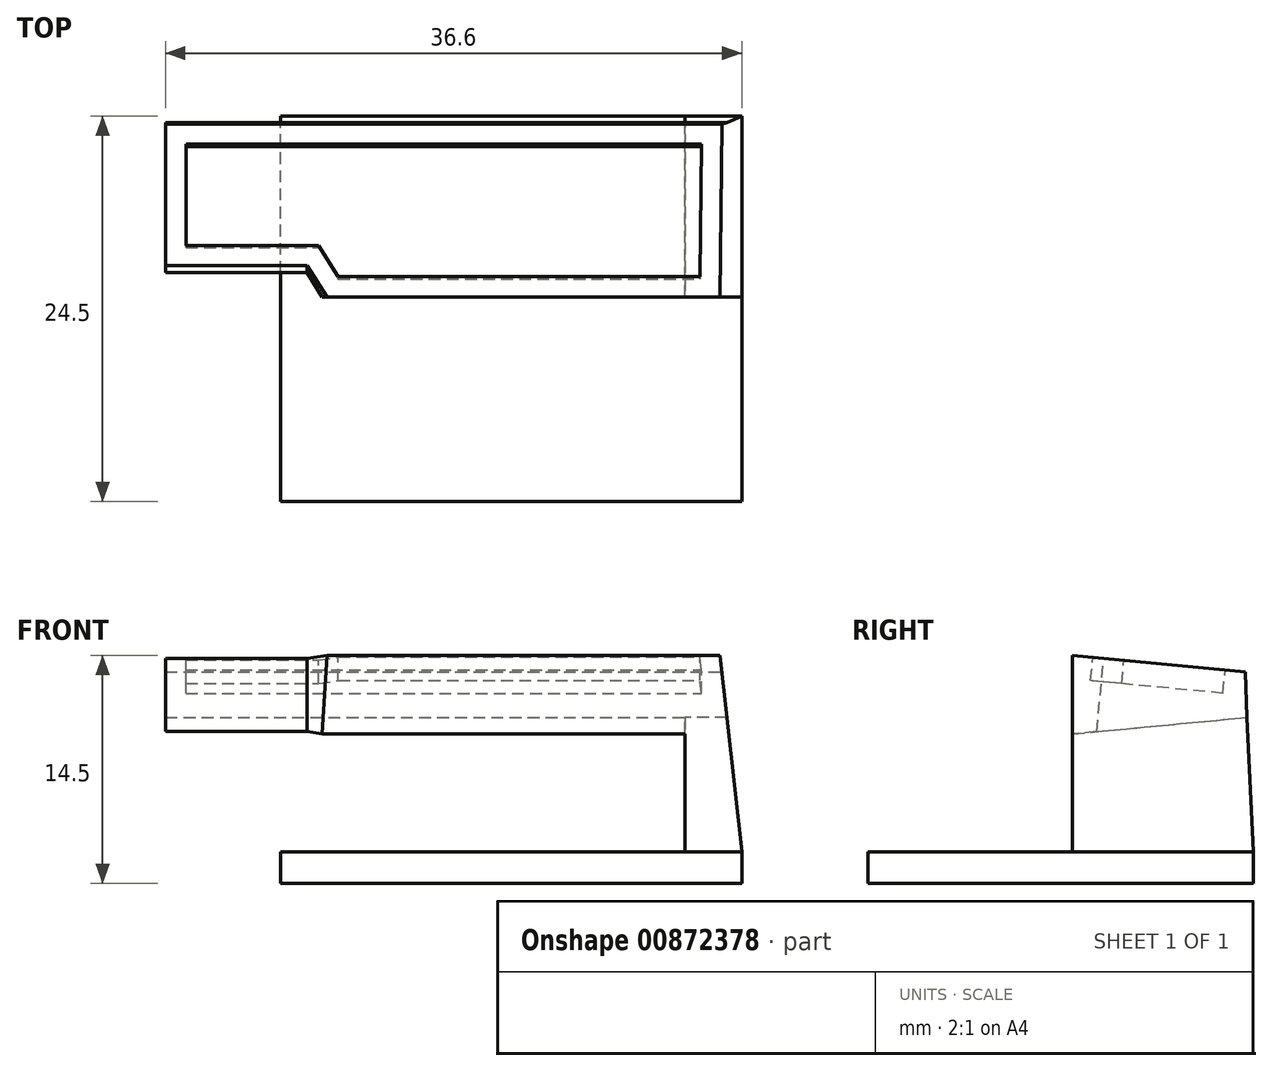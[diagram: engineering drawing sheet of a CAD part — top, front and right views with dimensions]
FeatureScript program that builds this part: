
annotation { "Feature Type Name" : "Feature", "Feature Type Description" : "" }
export const myFeature = defineFeature(function(context is Context, id is Id, definition is map)
    precondition{}
    {
        {
            var Q0;
            Q0=qCreatedBy(makeId("Top.planeOp"),FACE);
            var sketch = newSketch(context, id + "F0", { "sketchPlane" : qUnion([Q0])});
            skLineSegment(sketch, "E0.bottom", {"start": v(0, 0) * mm, "end": v(29.3, 0) * mm});
            skLineSegment(sketch, "E0.top", {"start": v(0, 24.5) * mm, "end": v(29.3, 24.5) * mm});
            skLineSegment(sketch, "E0.left", {"start": v(0, 0) * mm, "end": v(0, 24.5) * mm});
            skLineSegment(sketch, "E0.right", {"start": v(29.3, 0) * mm, "end": v(29.3, 24.5) * mm});
            skSolve(sketch);
        }
        {
            var Q0;
            Q0 = qSketchRegion(id + "F0", true);
            extrude(context, id + "F1", {"entities" : qUnion([Q0]), "depth" : 2 * mm, "offsetDistance" : 25 * mm});
        }
        {
            var Q0;
            Q0=makeQuery(id+"F1.opExtrude","CAP_FACE",FACE,{"disambiguationData":[OSD([sQuery(id+"F0.wireOp",EDGE,"E0.bottom"),sQuery(id+"F0.wireOp",EDGE,"E0.top"),sQuery(id+"F0.wireOp",EDGE,"E0.left"),sQuery(id+"F0.wireOp",EDGE,"E0.right")])],"isStart":false});
            var sketch = newSketch(context, id + "F2", { "sketchPlane" : qUnion([Q0])});
            skLineSegment(sketch, "E1.bottom", {"start": v(29.3, 24.5) * mm, "end": v(25.7, 24.5) * mm});
            skLineSegment(sketch, "E1.top", {"start": v(29.3, 13) * mm, "end": v(25.7, 13) * mm});
            skLineSegment(sketch, "E1.left", {"start": v(29.3, 24.5) * mm, "end": v(29.3, 13) * mm});
            skLineSegment(sketch, "E1.right", {"start": v(25.7, 24.5) * mm, "end": v(25.7, 13) * mm});
            skSolve(sketch);
        }
        {
            var Q0;
            {var subQ4=sQuery(id+"F2.wireOp",EDGE,"E1.top");Q0=makeQuery(id+"F2.imprint","IMPRINT",FACE,{"disambiguationData":[TD([[makeQuery(id+"F2.imprint","IMPRINT",EDGE,{"derivedFrom":subQ4}),1.0]])]});}
            cPlane(context, id + "F3", {"entities" : qUnion([Q0]), "cplaneType" : CPlaneType.OFFSET, "offset" : 10 * mm, "width" : 150 * mm, "height" : 150 * mm});
        }
        {
            var Q0;
            Q0=qCreatedBy(id+"F3.planeOp",FACE);
            var sketch = newSketch(context, id + "F4", { "sketchPlane" : qUnion([Q0])});
            skLineSegment(sketch, "E2.bottom", {"start": v(28.2, 24) * mm, "end": v(25.7, 24) * mm});
            skLineSegment(sketch, "E2.top", {"start": v(28.2, 13) * mm, "end": v(25.7, 13) * mm});
            skLineSegment(sketch, "E2.left", {"start": v(28.2, 24) * mm, "end": v(28.2, 13) * mm});
            skLineSegment(sketch, "E2.right", {"start": v(25.7, 24) * mm, "end": v(25.7, 13) * mm});
            skSolve(sketch);
        }
        {
            var Q1;
            Q1 = qSketchRegion(id + "F4", true);
            var Q2;
            Q2 = qSketchRegion(id + "F2", true);
            loft(context, id + "F5", {"operationType" : NewBodyOperationType.ADD, "sheetProfilesArray" : [{ "sheetProfileEntities" : qUnion([Q1]) }, { "sheetProfileEntities" : qUnion([Q2]) }]});
        }
        {
            var Q0;
            Q0=makeQuery(id+"F5.opLoft","SWEPT_FACE",FACE,{"disambiguationData":[OSD([sQuery(id+"F0.wireOp",EDGE,"E0.top"),sQuery(id+"F2.wireOp",EDGE,"E1.bottom"),sQuery(id+"F2.wireOp",EDGE,"E1.top"),sQuery(id+"F2.wireOp",EDGE,"E1.right"),sQuery(id+"F4.wireOp",EDGE,"E2.bottom"),sQuery(id+"F4.wireOp",EDGE,"E2.top"),sQuery(id+"F4.wireOp",EDGE,"E2.right")])]});
            var sketch = newSketch(context, id + "F6", { "sketchPlane" : qUnion([Q0])});
            skLineSegment(sketch, "E3", {"start": v(-13, 12) * mm, "end": v(-13, 9.5) * mm});
            skLineSegment(sketch, "E4", {"start": v(-13, 14.5) * mm, "end": v(-13, 12) * mm});
            skLineSegment(sketch, "E5", {"start": v(-13, 9.5) * mm, "end": v(-24.07, 10.55) * mm});
            skLineSegment(sketch, "E6", {"start": v(-24.07, 10.55) * mm, "end": v(-24, 13.45) * mm});
            skLineSegment(sketch, "E7", {"start": v(-24, 13.45) * mm, "end": v(-13, 14.5) * mm});
            skSolve(sketch);
        }
        {
            var Q0;
            Q0 = qSketchRegion(id + "F6", true);
            extrude(context, id + "F7", {"entities" : qUnion([Q0]), "operationType" : NewBodyOperationType.ADD, "depth" : 33 * mm, "offsetDistance" : 25 * mm});
        }
        {
            var Q0;
            Q0=makeQuery(id+"F7.opExtrude","CAP_FACE",FACE,{"disambiguationData":[OSD([sQuery(id+"F6.wireOp",EDGE,"E3"),sQuery(id+"F6.wireOp",EDGE,"E4"),sQuery(id+"F6.wireOp",EDGE,"E5"),sQuery(id+"F6.wireOp",EDGE,"E6"),sQuery(id+"F6.wireOp",EDGE,"E7")])],"isStart":true});
            var Q1;
            Q1=makeQuery(id+"F5.opLoft","SWEPT_FACE",FACE,{"disambiguationData":[OSD([sQuery(id+"F0.wireOp",EDGE,"E0.right"),sQuery(id+"F2.wireOp",EDGE,"E1.bottom"),sQuery(id+"F2.wireOp",EDGE,"E1.top"),sQuery(id+"F2.wireOp",EDGE,"E1.left"),sQuery(id+"F4.wireOp",EDGE,"E2.bottom"),sQuery(id+"F4.wireOp",EDGE,"E2.top"),sQuery(id+"F4.wireOp",EDGE,"E2.left")])]});
            extrude(context, id + "F8", {"entities" : qUnion([Q0]), "operationType" : NewBodyOperationType.ADD, "endBound" : BoundingType.UP_TO_SURFACE, "depth" : 25 * mm, "endBoundEntityFace" : qUnion([Q1]), "offsetDistance" : 25 * mm});
        }
        {
            var Q0;
            {var subQ0=sQuery(id+"F6.wireOp",EDGE,"E7");Q0=makeQuery(id+"F8.boolean.opBoolean","MERGE",FACE,{"derivedFrom":[makeQuery(id+"F7.opExtrude","SWEPT_FACE",FACE,{"disambiguationData":[OSD([subQ0])]}),makeQuery(id+"F8.opExtrude","SWEPT_FACE",FACE,{"disambiguationData":[OSD([subQ0])]})]});}
            var sketch = newSketch(context, id + "F9", { "sketchPlane" : qUnion([Q0])});
            skLineSegment(sketch, "E8", {"start": v(-7.3, 11.56) * mm, "end": v(-7.3, 13.56) * mm});
            skLineSegment(sketch, "E9", {"start": v(-7.3, 13.56) * mm, "end": v(1.7, 13.56) * mm});
            skLineSegment(sketch, "E10", {"start": v(1.7, 13.56) * mm, "end": v(2.95, 11.56) * mm});
            skLineSegment(sketch, "E11", {"start": v(2.95, 11.56) * mm, "end": v(-7.3, 11.56) * mm});
            skSolve(sketch);
        }
        {
            var Q0;
            Q0 = qSketchRegion(id + "F9", true);
            var Q1;
            Q1=makeQuery(id+"F7.opExtrude","SWEPT_FACE",FACE,{"disambiguationData":[OSD([sQuery(id+"F6.wireOp",EDGE,"E5")])]});
            extrude(context, id + "F10", {"entities" : qUnion([Q0]), "operationType" : NewBodyOperationType.REMOVE, "endBound" : BoundingType.UP_TO_SURFACE, "oppositeDirection" : true, "depth" : 25 * mm, "endBoundEntityFace" : qUnion([Q1]), "offsetDistance" : 25 * mm});
        }
        {
            var Q0;
            {var subQ0=sQuery(id+"F6.wireOp",EDGE,"E7");Q0=makeQuery(id+"F8.boolean.opBoolean","MERGE",FACE,{"derivedFrom":[makeQuery(id+"F7.opExtrude","SWEPT_FACE",FACE,{"disambiguationData":[OSD([subQ0])]}),makeQuery(id+"F8.opExtrude","SWEPT_FACE",FACE,{"disambiguationData":[OSD([subQ0])]})]});}
            var sketch = newSketch(context, id + "F11", { "sketchPlane" : qUnion([Q0])});
            skLineSegment(sketch, "E12.0", {"start": v(-6, 21.31) * mm, "end": v(-6, 14.86) * mm});
            skLineSegment(sketch, "E12.1", {"start": v(2.42, 14.86) * mm, "end": v(3.67, 12.86) * mm});
            skLineSegment(sketch, "E12.2", {"start": v(3.67, 12.86) * mm, "end": v(26.64, 12.86) * mm});
            skLineSegment(sketch, "E12.3", {"start": v(-6, 14.86) * mm, "end": v(2.42, 14.86) * mm});
            skLineSegment(sketch, "E12.4", {"start": v(26.73, 21.31) * mm, "end": v(26.64, 12.86) * mm});
            skLineSegment(sketch, "E12.5", {"start": v(-6, 21.31) * mm, "end": v(26.73, 21.31) * mm});
            skSolve(sketch);
        }
        {
            var Q0;
            Q0 = qSketchRegion(id + "F11", true);
            extrude(context, id + "F12", {"entities" : qUnion([Q0]), "operationType" : NewBodyOperationType.REMOVE, "oppositeDirection" : true, "depth" : 1.5 * mm, "offsetDistance" : 25 * mm});
        }
    });
